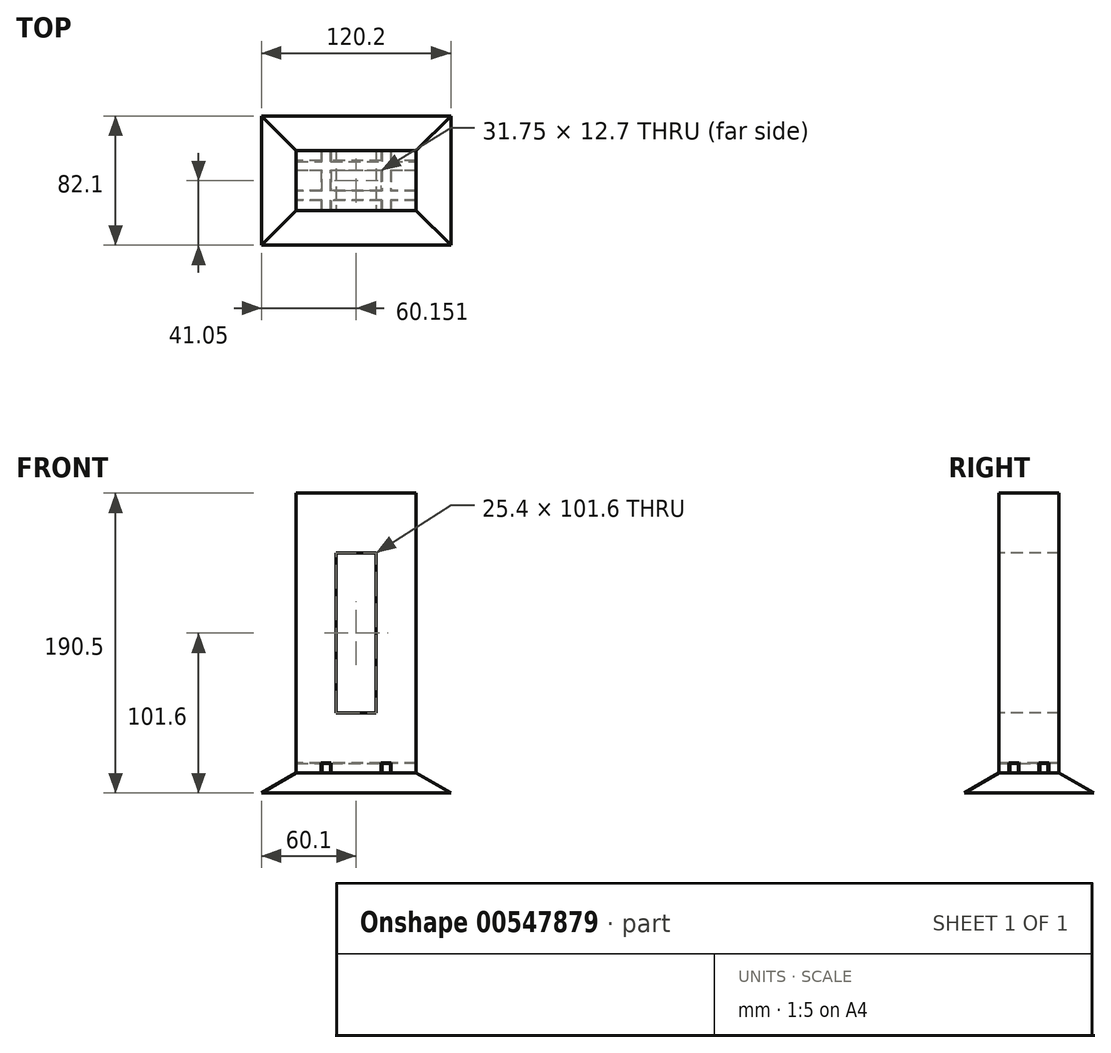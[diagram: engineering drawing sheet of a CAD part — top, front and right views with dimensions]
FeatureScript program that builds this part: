
annotation { "Feature Type Name" : "Feature", "Feature Type Description" : "" }
export const myFeature = defineFeature(function(context is Context, id is Id, definition is map)
    precondition{}
    {
        {
            var Q0;
            Q0=qCreatedBy(makeId("Front.planeOp"),FACE);
            var sketch = newSketch(context, id + "F0", { "sketchPlane" : qUnion([Q0])});
            skLineSegment(sketch, "E0.bottom", {"start": v(0, 0) * mm, "end": v(76.2, 0) * mm});
            skLineSegment(sketch, "E0.top", {"start": v(0, 177.8) * mm, "end": v(76.2, 177.8) * mm});
            skLineSegment(sketch, "E0.left", {"start": v(0, 0) * mm, "end": v(0, 177.8) * mm});
            skLineSegment(sketch, "E0.right", {"start": v(76.2, 0) * mm, "end": v(76.2, 177.8) * mm});
            skLineSegment(sketch, "E1.bottom", {"start": v(25.4, 139.7) * mm, "end": v(50.8, 139.7) * mm});
            skLineSegment(sketch, "E1.top", {"start": v(25.4, 38.1) * mm, "end": v(50.8, 38.1) * mm});
            skLineSegment(sketch, "E1.left", {"start": v(25.4, 139.7) * mm, "end": v(25.4, 38.1) * mm});
            skLineSegment(sketch, "E1.right", {"start": v(50.8, 139.7) * mm, "end": v(50.8, 38.1) * mm});
            skLineSegment(sketch, "E2.bottom", {"start": v(15.93, 0) * mm, "end": v(22.28, 0) * mm});
            skLineSegment(sketch, "E2.top", {"start": v(15.93, 6.35) * mm, "end": v(22.28, 6.35) * mm});
            skLineSegment(sketch, "E2.left", {"start": v(15.93, 0) * mm, "end": v(15.93, 6.35) * mm});
            skLineSegment(sketch, "E2.right", {"start": v(22.28, 0) * mm, "end": v(22.28, 6.35) * mm});
            skLineSegment(sketch, "E3.bottom", {"start": v(54.03, 0) * mm, "end": v(60.38, 0) * mm});
            skLineSegment(sketch, "E3.top", {"start": v(54.03, 6.35) * mm, "end": v(60.38, 6.35) * mm});
            skLineSegment(sketch, "E3.left", {"start": v(54.03, 0) * mm, "end": v(54.03, 6.35) * mm});
            skLineSegment(sketch, "E3.right", {"start": v(60.38, 0) * mm, "end": v(60.38, 6.35) * mm});
            skSolve(sketch);
        }
        {
            var Q0;
            Q0=makeQuery(id+"F0.imprint","IMPRINT",FACE,{"disambiguationData":[TD([[makeQuery(id+"F0.imprint","IMPRINT",EDGE,{"derivedFrom":sQuery(id+"F0.wireOp",EDGE,"E0.bottom")}),1.0]])]});
            extrude(context, id + "F1", {"entities" : qUnion([Q0]), "oppositeDirection" : true, "depth" : 38.1 * mm, "offsetDistance" : 25.4 * mm});
        }
        {
            var Q0;
            Q0=makeQuery(id+"F1.opExtrude","SWEPT_FACE",FACE,{"disambiguationData":[OSD([sQuery(id+"F0.wireOp",EDGE,"E0.left")])]});
            var sketch = newSketch(context, id + "F2", { "sketchPlane" : qUnion([Q0])});
            skLineSegment(sketch, "E4.bottom", {"start": v(-31.75, 0) * mm, "end": v(-25.4, 0) * mm});
            skLineSegment(sketch, "E4.top", {"start": v(-31.75, 6.35) * mm, "end": v(-25.4, 6.35) * mm});
            skLineSegment(sketch, "E4.left", {"start": v(-31.75, 0) * mm, "end": v(-31.75, 6.35) * mm});
            skLineSegment(sketch, "E4.right", {"start": v(-25.4, 0) * mm, "end": v(-25.4, 6.35) * mm});
            skLineSegment(sketch, "E5.bottom", {"start": v(-12.7, 0) * mm, "end": v(-6.35, 0) * mm});
            skLineSegment(sketch, "E5.top", {"start": v(-12.7, 6.35) * mm, "end": v(-6.35, 6.35) * mm});
            skLineSegment(sketch, "E5.left", {"start": v(-12.7, 0) * mm, "end": v(-12.7, 6.35) * mm});
            skLineSegment(sketch, "E5.right", {"start": v(-6.35, 0) * mm, "end": v(-6.35, 6.35) * mm});
            skSolve(sketch);
        }
        {
            var Q0;
            Q0=makeQuery(id+"F2.imprint","IMPRINT",FACE,{"disambiguationData":[TD([[makeQuery(id+"F2.imprint","IMPRINT",EDGE,{"derivedFrom":sQuery(id+"F2.wireOp",EDGE,"E4.bottom")}),1.0]])]});
            var Q1;
            Q1=makeQuery(id+"F2.imprint","IMPRINT",FACE,{"disambiguationData":[TD([[makeQuery(id+"F2.imprint","IMPRINT",EDGE,{"derivedFrom":sQuery(id+"F2.wireOp",EDGE,"E5.bottom")}),1.0]])]});
            extrude(context, id + "F3", {"entities" : qUnion([Q0, Q1]), "operationType" : NewBodyOperationType.REMOVE, "endBound" : BoundingType.THROUGH_ALL, "oppositeDirection" : true, "depth" : 25.4 * mm, "offsetDistance" : 25.4 * mm});
        }
        {
            var Q0;
            Q0=qCreatedBy(makeId("Top.planeOp"),FACE);
            var sketch = newSketch(context, id + "F4", { "sketchPlane" : qUnion([Q0])});
            skLineSegment(sketch, "E6.0.0", {"start": v(54.03, 0) * mm, "end": v(54.03, 6.35) * mm, "construction": true});
            skLineSegment(sketch, "E6.0.1", {"start": v(54.03, 6.35) * mm, "end": v(22.28, 6.35) * mm, "construction": true});
            skLineSegment(sketch, "E6.0.2", {"start": v(22.28, 6.35) * mm, "end": v(22.28, 0) * mm, "construction": true});
            skLineSegment(sketch, "E6.0.3", {"start": v(22.28, 0) * mm, "end": v(15.93, 0) * mm, "construction": true});
            skLineSegment(sketch, "E6.0.4", {"start": v(15.93, 0) * mm, "end": v(15.93, 6.35) * mm, "construction": true});
            skLineSegment(sketch, "E6.0.5", {"start": v(15.93, 6.35) * mm, "end": v(0, 6.35) * mm, "construction": true});
            skLineSegment(sketch, "E6.0.6", {"start": v(0, 6.35) * mm, "end": v(0, 12.7) * mm, "construction": true});
            skLineSegment(sketch, "E6.0.7", {"start": v(0, 12.7) * mm, "end": v(15.93, 12.7) * mm, "construction": true});
            skLineSegment(sketch, "E6.0.8", {"start": v(15.93, 12.7) * mm, "end": v(15.93, 25.4) * mm, "construction": true});
            skLineSegment(sketch, "E6.0.9", {"start": v(15.93, 25.4) * mm, "end": v(0, 25.4) * mm, "construction": true});
            skLineSegment(sketch, "E6.0.10", {"start": v(0, 25.4) * mm, "end": v(0, 31.75) * mm, "construction": true});
            skLineSegment(sketch, "E6.0.11", {"start": v(0, 31.75) * mm, "end": v(15.93, 31.75) * mm, "construction": true});
            skLineSegment(sketch, "E6.0.12", {"start": v(15.93, 31.75) * mm, "end": v(15.93, 38.1) * mm, "construction": true});
            skLineSegment(sketch, "E6.0.13", {"start": v(15.93, 38.1) * mm, "end": v(22.28, 38.1) * mm, "construction": true});
            skLineSegment(sketch, "E6.0.14", {"start": v(22.28, 38.1) * mm, "end": v(22.28, 31.75) * mm, "construction": true});
            skLineSegment(sketch, "E6.0.15", {"start": v(22.28, 31.75) * mm, "end": v(54.03, 31.75) * mm, "construction": true});
            skLineSegment(sketch, "E6.0.16", {"start": v(54.03, 31.75) * mm, "end": v(54.03, 38.1) * mm, "construction": true});
            skLineSegment(sketch, "E6.0.17", {"start": v(54.03, 38.1) * mm, "end": v(60.38, 38.1) * mm, "construction": true});
            skLineSegment(sketch, "E6.0.18", {"start": v(60.38, 38.1) * mm, "end": v(60.38, 31.75) * mm, "construction": true});
            skLineSegment(sketch, "E6.0.19", {"start": v(60.38, 31.75) * mm, "end": v(76.2, 31.75) * mm, "construction": true});
            skLineSegment(sketch, "E6.0.20", {"start": v(76.2, 31.75) * mm, "end": v(76.2, 25.4) * mm, "construction": true});
            skLineSegment(sketch, "E6.0.21", {"start": v(76.2, 25.4) * mm, "end": v(60.38, 25.4) * mm, "construction": true});
            skLineSegment(sketch, "E6.0.22", {"start": v(60.38, 25.4) * mm, "end": v(60.38, 12.7) * mm, "construction": true});
            skLineSegment(sketch, "E6.0.23", {"start": v(60.38, 12.7) * mm, "end": v(76.2, 12.7) * mm, "construction": true});
            skLineSegment(sketch, "E6.0.24", {"start": v(76.2, 12.7) * mm, "end": v(76.2, 6.35) * mm, "construction": true});
            skLineSegment(sketch, "E6.0.25", {"start": v(76.2, 6.35) * mm, "end": v(60.38, 6.35) * mm, "construction": true});
            skLineSegment(sketch, "E6.0.26", {"start": v(60.38, 6.35) * mm, "end": v(60.38, 0) * mm, "construction": true});
            skLineSegment(sketch, "E6.0.27", {"start": v(60.38, 0) * mm, "end": v(54.03, 0) * mm, "construction": true});
            skLineSegment(sketch, "E7.0.0", {"start": v(54.03, 25.4) * mm, "end": v(54.03, 12.7) * mm, "construction": true});
            skLineSegment(sketch, "E7.0.1", {"start": v(54.03, 12.7) * mm, "end": v(22.28, 12.7) * mm, "construction": true});
            skLineSegment(sketch, "E7.0.2", {"start": v(22.28, 12.7) * mm, "end": v(22.28, 25.4) * mm, "construction": true});
            skLineSegment(sketch, "E7.0.3", {"start": v(22.28, 25.4) * mm, "end": v(54.03, 25.4) * mm, "construction": true});
            skLineSegment(sketch, "E8", {"start": v(19.1, 0) * mm, "end": v(19.1, 38.1) * mm, "construction": true});
            skLineSegment(sketch, "E9", {"start": v(57.2, 0) * mm, "end": v(57.2, 38.1) * mm, "construction": true});
            skLineSegment(sketch, "E10", {"start": v(0, 9.53) * mm, "end": v(76.2, 9.53) * mm, "construction": true});
            skLineSegment(sketch, "E11", {"start": v(0, 28.57) * mm, "end": v(76.2, 28.57) * mm, "construction": true});
            skLineSegment(sketch, "E12.bottom", {"start": v(16.3, 0) * mm, "end": v(21.9, 0) * mm});
            skLineSegment(sketch, "E12.top", {"start": v(16.3, 38.1) * mm, "end": v(21.9, 38.1) * mm});
            skLineSegment(sketch, "E12.left", {"start": v(16.3, 0) * mm, "end": v(16.3, 38.1) * mm});
            skLineSegment(sketch, "E12.right", {"start": v(21.9, 0) * mm, "end": v(21.9, 38.1) * mm});
            skLineSegment(sketch, "E13.bottom", {"start": v(54.4, 38.1) * mm, "end": v(60, 38.1) * mm});
            skLineSegment(sketch, "E13.top", {"start": v(54.4, 0) * mm, "end": v(60, 0) * mm});
            skLineSegment(sketch, "E13.left", {"start": v(54.4, 38.1) * mm, "end": v(54.4, 0) * mm});
            skLineSegment(sketch, "E13.right", {"start": v(60, 38.1) * mm, "end": v(60, 0) * mm});
            skLineSegment(sketch, "E14.bottom", {"start": v(76.2, 6.73) * mm, "end": v(0, 6.73) * mm});
            skLineSegment(sketch, "E14.top", {"start": v(76.2, 12.32) * mm, "end": v(0, 12.32) * mm});
            skLineSegment(sketch, "E14.left", {"start": v(76.2, 6.73) * mm, "end": v(76.2, 12.32) * mm});
            skLineSegment(sketch, "E14.right", {"start": v(0, 6.73) * mm, "end": v(0, 12.32) * mm});
            skLineSegment(sketch, "E15.bottom", {"start": v(0, 25.78) * mm, "end": v(76.2, 25.78) * mm});
            skLineSegment(sketch, "E15.top", {"start": v(0, 31.12) * mm, "end": v(76.2, 31.12) * mm});
            skLineSegment(sketch, "E15.left", {"start": v(0, 25.78) * mm, "end": v(0, 31.12) * mm});
            skLineSegment(sketch, "E15.right", {"start": v(76.2, 25.78) * mm, "end": v(76.2, 31.12) * mm});
            skSolve(sketch);
        }
        {
            var Q0;
            {var subQ0=sQuery(id+"F4.wireOp",EDGE,"E12.bottom");Q0=makeQuery(id+"F4.imprint","IMPRINT",FACE,{"disambiguationData":[TD([[makeQuery(id+"F4.imprint","IMPRINT",EDGE,{"derivedFrom":subQ0}),1.0]])]});}
            var Q1;
            {var subQ0=sQuery(id+"F4.wireOp",EDGE,"E14.bottom");var subQ1=sQuery(id+"F4.wireOp",EDGE,"E12.left");var subQ2=makeQuery(id+"F4.imprint","INTERSECT",VERTEX,{"derivedFrom":[subQ1,subQ0]});Q1=makeQuery(id+"F4.imprint","IMPRINT",FACE,{"disambiguationData":[TD([[makeQuery(id+"F4.imprint","IMPRINT",EDGE,{"disambiguationData":[TD([[subQ2,-1.0]])],"derivedFrom":subQ1}),-1.0]])]});}
            var Q2;
            {var subQ5=sQuery(id+"F4.wireOp",EDGE,"E14.right");Q2=makeQuery(id+"F4.imprint","IMPRINT",FACE,{"disambiguationData":[TD([[makeQuery(id+"F4.imprint","IMPRINT",EDGE,{"derivedFrom":subQ5}),-1.0]])]});}
            var Q3;
            {var subQ0=sQuery(id+"F4.wireOp",EDGE,"E14.top");var subQ1=sQuery(id+"F4.wireOp",EDGE,"E12.left");var subQ2=makeQuery(id+"F4.imprint","INTERSECT",VERTEX,{"derivedFrom":[subQ1,subQ0]});Q3=makeQuery(id+"F4.imprint","IMPRINT",FACE,{"disambiguationData":[TD([[makeQuery(id+"F4.imprint","IMPRINT",EDGE,{"disambiguationData":[TD([[subQ2,-1.0]])],"derivedFrom":subQ1}),-1.0]])]});}
            var Q4;
            {var subQ0=sQuery(id+"F4.wireOp",EDGE,"E14.bottom");var subQ1=sQuery(id+"F4.wireOp",EDGE,"E12.right");var subQ2=makeQuery(id+"F4.imprint","INTERSECT",VERTEX,{"derivedFrom":[subQ1,subQ0]});Q4=makeQuery(id+"F4.imprint","IMPRINT",FACE,{"disambiguationData":[TD([[makeQuery(id+"F4.imprint","IMPRINT",EDGE,{"disambiguationData":[TD([[subQ2,-1.0]])],"derivedFrom":subQ1}),-1.0]])]});}
            var Q5;
            {var subQ0=sQuery(id+"F4.wireOp",EDGE,"E14.bottom");var subQ1=sQuery(id+"F4.wireOp",EDGE,"E13.left");var subQ2=makeQuery(id+"F4.imprint","INTERSECT",VERTEX,{"derivedFrom":[subQ1,subQ0]});Q5=makeQuery(id+"F4.imprint","IMPRINT",FACE,{"disambiguationData":[TD([[makeQuery(id+"F4.imprint","IMPRINT",EDGE,{"disambiguationData":[TD([[subQ2,1.0]])],"derivedFrom":subQ1}),1.0]])]});}
            var Q6;
            {var subQ0=sQuery(id+"F4.wireOp",EDGE,"E13.top");Q6=makeQuery(id+"F4.imprint","IMPRINT",FACE,{"disambiguationData":[TD([[makeQuery(id+"F4.imprint","IMPRINT",EDGE,{"derivedFrom":subQ0}),1.0]])]});}
            var Q7;
            {var subQ5=sQuery(id+"F4.wireOp",EDGE,"E14.left");Q7=makeQuery(id+"F4.imprint","IMPRINT",FACE,{"disambiguationData":[TD([[makeQuery(id+"F4.imprint","IMPRINT",EDGE,{"derivedFrom":subQ5}),1.0]])]});}
            var Q8;
            {var subQ0=sQuery(id+"F4.wireOp",EDGE,"E15.bottom");var subQ1=sQuery(id+"F4.wireOp",EDGE,"E13.left");var subQ2=makeQuery(id+"F4.imprint","INTERSECT",VERTEX,{"derivedFrom":[subQ1,subQ0]});Q8=makeQuery(id+"F4.imprint","IMPRINT",FACE,{"disambiguationData":[TD([[makeQuery(id+"F4.imprint","IMPRINT",EDGE,{"disambiguationData":[TD([[subQ2,-1.0]])],"derivedFrom":subQ1}),1.0]])]});}
            var Q9;
            {var subQ0=sQuery(id+"F4.wireOp",EDGE,"E15.top");var subQ1=sQuery(id+"F4.wireOp",EDGE,"E13.left");var subQ2=makeQuery(id+"F4.imprint","INTERSECT",VERTEX,{"derivedFrom":[subQ1,subQ0]});Q9=makeQuery(id+"F4.imprint","IMPRINT",FACE,{"disambiguationData":[TD([[makeQuery(id+"F4.imprint","IMPRINT",EDGE,{"disambiguationData":[TD([[subQ2,-1.0]])],"derivedFrom":subQ1}),1.0]])]});}
            var Q10;
            {var subQ5=sQuery(id+"F4.wireOp",EDGE,"E15.right");Q10=makeQuery(id+"F4.imprint","IMPRINT",FACE,{"disambiguationData":[TD([[makeQuery(id+"F4.imprint","IMPRINT",EDGE,{"derivedFrom":subQ5}),1.0]])]});}
            var Q11;
            {var subQ0=sQuery(id+"F4.wireOp",EDGE,"E13.bottom");Q11=makeQuery(id+"F4.imprint","IMPRINT",FACE,{"disambiguationData":[TD([[makeQuery(id+"F4.imprint","IMPRINT",EDGE,{"derivedFrom":subQ0}),-1.0]])]});}
            var Q12;
            {var subQ0=sQuery(id+"F4.wireOp",EDGE,"E15.top");var subQ1=sQuery(id+"F4.wireOp",EDGE,"E12.right");var subQ2=makeQuery(id+"F4.imprint","INTERSECT",VERTEX,{"derivedFrom":[subQ1,subQ0]});Q12=makeQuery(id+"F4.imprint","IMPRINT",FACE,{"disambiguationData":[TD([[makeQuery(id+"F4.imprint","IMPRINT",EDGE,{"disambiguationData":[TD([[subQ2,1.0]])],"derivedFrom":subQ1}),-1.0]])]});}
            var Q13;
            {var subQ0=sQuery(id+"F4.wireOp",EDGE,"E15.bottom");var subQ1=sQuery(id+"F4.wireOp",EDGE,"E12.left");var subQ2=makeQuery(id+"F4.imprint","INTERSECT",VERTEX,{"derivedFrom":[subQ1,subQ0]});Q13=makeQuery(id+"F4.imprint","IMPRINT",FACE,{"disambiguationData":[TD([[makeQuery(id+"F4.imprint","IMPRINT",EDGE,{"disambiguationData":[TD([[subQ2,-1.0]])],"derivedFrom":subQ1}),-1.0]])]});}
            var Q14;
            {var subQ0=sQuery(id+"F4.wireOp",EDGE,"E12.top");Q14=makeQuery(id+"F4.imprint","IMPRINT",FACE,{"disambiguationData":[TD([[makeQuery(id+"F4.imprint","IMPRINT",EDGE,{"derivedFrom":subQ0}),-1.0]])]});}
            var Q15;
            {var subQ5=sQuery(id+"F4.wireOp",EDGE,"E15.left");Q15=makeQuery(id+"F4.imprint","IMPRINT",FACE,{"disambiguationData":[TD([[makeQuery(id+"F4.imprint","IMPRINT",EDGE,{"derivedFrom":subQ5}),-1.0]])]});}
            extrude(context, id + "F5", {"entities" : qUnion([Q0, Q1, Q2, Q3, Q4, Q5, Q6, Q7, Q8, Q9, Q10, Q11, Q12, Q13, Q14, Q15]), "depth" : 6.1 * mm, "offsetDistance" : 25.4 * mm});
        }
        {
            var Q0;
            Q0=makeQuery(id+"F5.opExtrude","CAP_FACE",FACE,{"disambiguationData":[OSD([sQuery(id+"F4.wireOp",EDGE,"E12.bottom"),sQuery(id+"F4.wireOp",EDGE,"E12.top"),sQuery(id+"F4.wireOp",EDGE,"E12.left"),sQuery(id+"F4.wireOp",EDGE,"E12.right"),sQuery(id+"F4.wireOp",EDGE,"E13.bottom"),sQuery(id+"F4.wireOp",EDGE,"E13.top"),sQuery(id+"F4.wireOp",EDGE,"E13.left"),sQuery(id+"F4.wireOp",EDGE,"E13.right"),sQuery(id+"F4.wireOp",EDGE,"E14.bottom"),sQuery(id+"F4.wireOp",EDGE,"E14.top"),sQuery(id+"F4.wireOp",EDGE,"E14.left"),sQuery(id+"F4.wireOp",EDGE,"E14.right"),sQuery(id+"F4.wireOp",EDGE,"E15.bottom"),sQuery(id+"F4.wireOp",EDGE,"E15.top"),sQuery(id+"F4.wireOp",EDGE,"E15.left"),sQuery(id+"F4.wireOp",EDGE,"E15.right")])],"isStart":true});
            var sketch = newSketch(context, id + "F6", { "sketchPlane" : qUnion([Q0])});
            skPoint(sketch, "E16.oppositeSnap0", {"position": v(76.2, -28.45) * mm});
            skLineSegment(sketch, "E16.bottom", {"start": v(0, 0) * mm, "end": v(76.2, 0) * mm});
            skLineSegment(sketch, "E16.top", {"start": v(0, -38.1) * mm, "end": v(76.2, -38.1) * mm});
            skLineSegment(sketch, "E16.left", {"start": v(0, 0) * mm, "end": v(0, -38.1) * mm});
            skLineSegment(sketch, "E16.right", {"start": v(76.2, 0) * mm, "end": v(76.2, -38.1) * mm});
            skSolve(sketch);
        }
        {
            var Q0;
            Q0 = qSketchRegion(id + "F6", true);
            extrude(context, id + "F7", {"entities" : qUnion([Q0]), "operationType" : NewBodyOperationType.ADD, "depth" : 12.7 * mm, "offsetDistance" : 25.4 * mm, "hasDraft" : true, "draftAngle" : 60 * degree});
        }
    });
